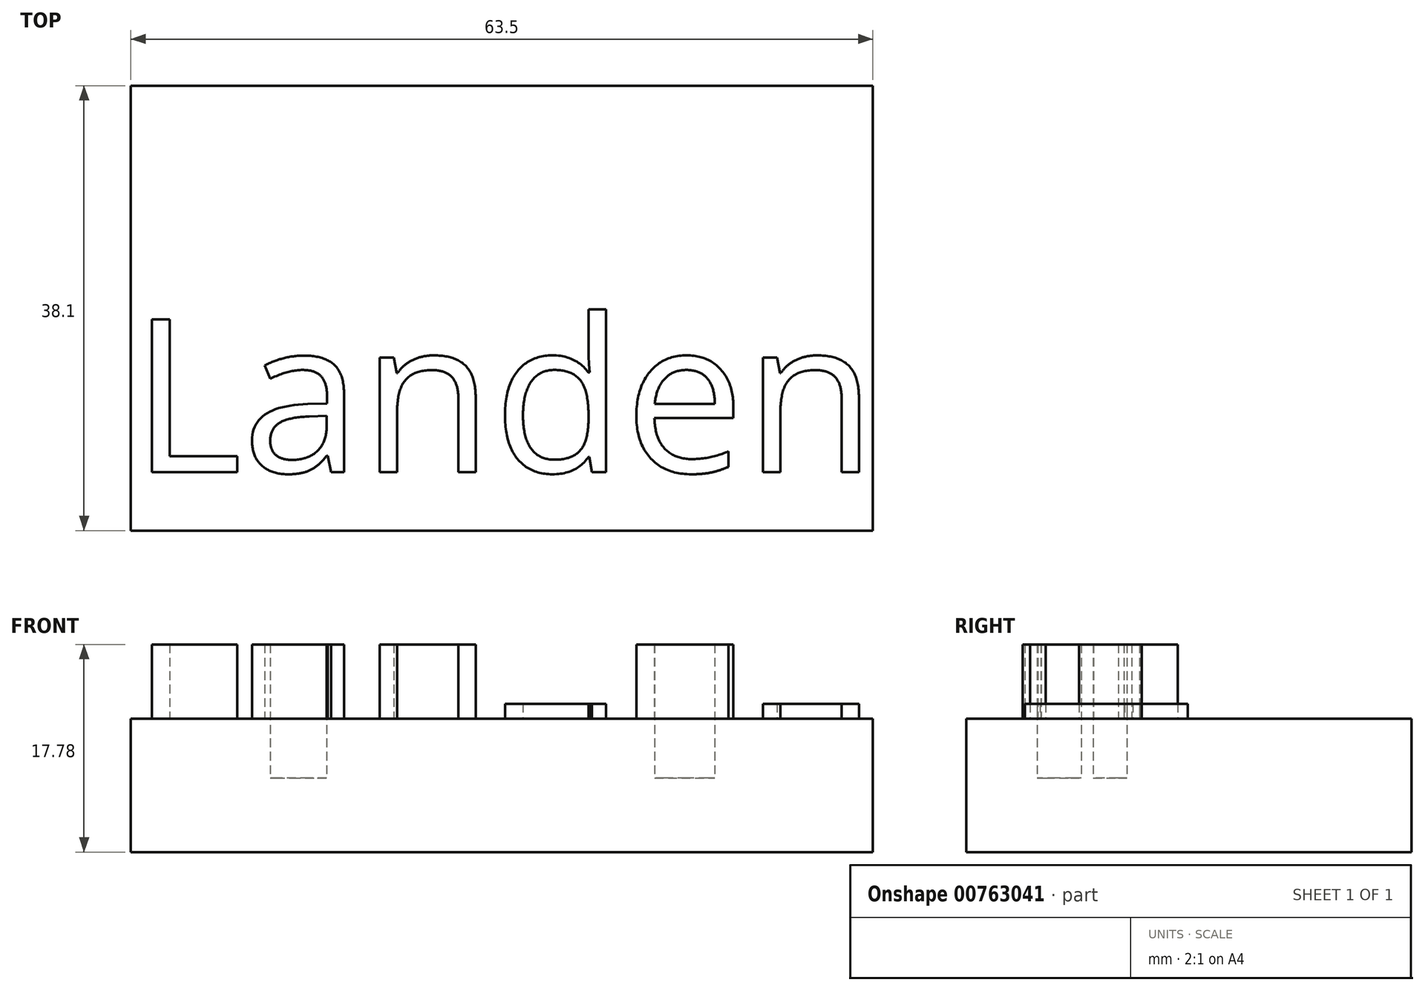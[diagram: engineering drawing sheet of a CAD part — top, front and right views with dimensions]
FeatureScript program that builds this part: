
annotation { "Feature Type Name" : "Feature", "Feature Type Description" : "" }
export const myFeature = defineFeature(function(context is Context, id is Id, definition is map)
    precondition{}
    {
        {
            var Q0;
            Q0=qCreatedBy(makeId("Top.planeOp"),FACE);
            var sketch = newSketch(context, id + "F0", { "sketchPlane" : qUnion([Q0])});
            skLineSegment(sketch, "E0.bottom", {"start": v(0, 0) * mm, "end": v(63.5, 0) * mm});
            skLineSegment(sketch, "E0.top", {"start": v(0, 38.1) * mm, "end": v(63.5, 38.1) * mm});
            skLineSegment(sketch, "E0.left", {"start": v(0, 0) * mm, "end": v(0, 38.1) * mm});
            skLineSegment(sketch, "E0.right", {"start": v(63.5, 0) * mm, "end": v(63.5, 38.1) * mm});
            skSolve(sketch);
        }
        {
            var Q0;
            Q0=makeQuery(id+"F0.imprint","IMPRINT",FACE,{"disambiguationData":[TD([[makeQuery(id+"F0.imprint","IMPRINT",EDGE,{"derivedFrom":sQuery(id+"F0.wireOp",EDGE,"E0.bottom")}),1.0]])]});
            extrude(context, id + "F1", {"entities" : qUnion([Q0]), "depth" : 6.35 * mm, "offsetDistance" : 25.4 * mm});
        }
        {
            var Q0;
            Q0=makeQuery(id+"F1.opExtrude","CAP_FACE",FACE,{"disambiguationData":[OSD([sQuery(id+"F0.wireOp",EDGE,"E0.bottom"),sQuery(id+"F0.wireOp",EDGE,"E0.top"),sQuery(id+"F0.wireOp",EDGE,"E0.left"),sQuery(id+"F0.wireOp",EDGE,"E0.right")])],"isStart":false});
            var sketch = newSketch(context, id + "F2", { "sketchPlane" : qUnion([Q0])});
            skText(sketch, "E1", { "text": "Landen", "fontName": "OpenSans-Regular.ttf"});
            const initialGuessF2  = {"E1": [0, 0.005, 1, 0, 0.01321]};
            skSetInitialGuess(sketch, initialGuessF2);
            skSolve(sketch);
        }
        {
            var Q0;
            Q0 = qSketchRegion(id + "F2", true);
            extrude(context, id + "F3", {"entities" : qUnion([Q0]), "operationType" : NewBodyOperationType.ADD, "depth" : 6.35 * mm, "offsetDistance" : 25.4 * mm});
        }
        {
            var Q0;
            Q0 = qSketchRegion(id + "F2", true);
            extrude(context, id + "F4", {"entities" : qUnion([Q0]), "operationType" : NewBodyOperationType.ADD, "depth" : 5.08 * mm, "offsetDistance" : 25.4 * mm});
        }
        {
            var Q0;
            Q0=makeQuery(id+"F3.opExtrude","CAP_FACE",FACE,{"disambiguationData":[OSD([sQuery(id+"F2.wireOp",EDGE,"E1.sketch_text.stroke-0"),sQuery(id+"F2.wireOp",EDGE,"E1.sketch_text.stroke-1"),sQuery(id+"F2.wireOp",EDGE,"E1.sketch_text.stroke-2"),sQuery(id+"F2.wireOp",EDGE,"E1.sketch_text.stroke-3"),sQuery(id+"F2.wireOp",EDGE,"E1.sketch_text.stroke-4"),sQuery(id+"F2.wireOp",EDGE,"E1.sketch_text.stroke-5")])],"isStart":false});
            var Q1;
            Q1=makeQuery(id+"F3.opExtrude","CAP_FACE",FACE,{"disambiguationData":[OSD([sQuery(id+"F2.wireOp",EDGE,"E1.sketch_text.stroke-6"),sQuery(id+"F2.wireOp",EDGE,"E1.sketch_text.stroke-7"),sQuery(id+"F2.wireOp",EDGE,"E1.sketch_text.stroke-8"),sQuery(id+"F2.wireOp",EDGE,"E1.sketch_text.stroke-9"),sQuery(id+"F2.wireOp",EDGE,"E1.sketch_text.stroke-10"),sQuery(id+"F2.wireOp",EDGE,"E1.sketch_text.stroke-11"),sQuery(id+"F2.wireOp",EDGE,"E1.sketch_text.stroke-12"),sQuery(id+"F2.wireOp",EDGE,"E1.sketch_text.stroke-13"),sQuery(id+"F2.wireOp",EDGE,"E1.sketch_text.stroke-14"),sQuery(id+"F2.wireOp",EDGE,"E1.sketch_text.stroke-15"),sQuery(id+"F2.wireOp",EDGE,"E1.sketch_text.stroke-16"),sQuery(id+"F2.wireOp",EDGE,"E1.sketch_text.stroke-17"),sQuery(id+"F2.wireOp",EDGE,"E1.sketch_text.stroke-18"),sQuery(id+"F2.wireOp",EDGE,"E1.sketch_text.stroke-19"),sQuery(id+"F2.wireOp",EDGE,"E1.sketch_text.stroke-20"),sQuery(id+"F2.wireOp",EDGE,"E1.sketch_text.stroke-21"),sQuery(id+"F2.wireOp",EDGE,"E1.sketch_text.stroke-22"),sQuery(id+"F2.wireOp",EDGE,"E1.sketch_text.stroke-23"),sQuery(id+"F2.wireOp",EDGE,"E1.sketch_text.stroke-24"),sQuery(id+"F2.wireOp",EDGE,"E1.sketch_text.stroke-25"),sQuery(id+"F2.wireOp",EDGE,"E1.sketch_text.stroke-26"),sQuery(id+"F2.wireOp",EDGE,"E1.sketch_text.stroke-27"),sQuery(id+"F2.wireOp",EDGE,"E1.sketch_text.stroke-28"),sQuery(id+"F2.wireOp",EDGE,"E1.sketch_text.stroke-29"),sQuery(id+"F2.wireOp",EDGE,"E1.sketch_text.stroke-30"),sQuery(id+"F2.wireOp",EDGE,"E1.sketch_text.stroke-31"),sQuery(id+"F2.wireOp",EDGE,"E1.sketch_text.stroke-32")])],"isStart":false});
            var Q2;
            {var subQ0=sQuery(id+"F0.wireOp",EDGE,"E0.left");var subQ1=sQuery(id+"F0.wireOp",EDGE,"E0.bottom");var subQ2=sQuery(id+"F0.wireOp",EDGE,"E0.right");var subQ3=sQuery(id+"F0.wireOp",EDGE,"E0.top");Q2=makeQuery(id+"F3.boolean.opBoolean","SPLIT",FACE,{"disambiguationData":[TD([makeQuery(id+"F1.opExtrude","SWEPT_FACE",FACE,{"disambiguationData":[OSD([subQ1])]})])],"derivedFrom":makeQuery(id+"F1.opExtrude","CAP_FACE",FACE,{"disambiguationData":[OSD([subQ1,subQ3,subQ0,subQ2])],"isStart":false})});}
            var Q3;
            Q3=makeQuery(id+"F3.opExtrude","CAP_FACE",FACE,{"disambiguationData":[OSD([sQuery(id+"F2.wireOp",EDGE,"E1.sketch_text.stroke-33"),sQuery(id+"F2.wireOp",EDGE,"E1.sketch_text.stroke-34"),sQuery(id+"F2.wireOp",EDGE,"E1.sketch_text.stroke-35"),sQuery(id+"F2.wireOp",EDGE,"E1.sketch_text.stroke-36"),sQuery(id+"F2.wireOp",EDGE,"E1.sketch_text.stroke-37"),sQuery(id+"F2.wireOp",EDGE,"E1.sketch_text.stroke-38"),sQuery(id+"F2.wireOp",EDGE,"E1.sketch_text.stroke-39"),sQuery(id+"F2.wireOp",EDGE,"E1.sketch_text.stroke-40"),sQuery(id+"F2.wireOp",EDGE,"E1.sketch_text.stroke-41"),sQuery(id+"F2.wireOp",EDGE,"E1.sketch_text.stroke-42"),sQuery(id+"F2.wireOp",EDGE,"E1.sketch_text.stroke-43"),sQuery(id+"F2.wireOp",EDGE,"E1.sketch_text.stroke-44"),sQuery(id+"F2.wireOp",EDGE,"E1.sketch_text.stroke-45"),sQuery(id+"F2.wireOp",EDGE,"E1.sketch_text.stroke-46"),sQuery(id+"F2.wireOp",EDGE,"E1.sketch_text.stroke-47"),sQuery(id+"F2.wireOp",EDGE,"E1.sketch_text.stroke-48"),sQuery(id+"F2.wireOp",EDGE,"E1.sketch_text.stroke-49")])],"isStart":false});
            var Q4;
            Q4=makeQuery(id+"F3.boolean.opBoolean","SPLIT",FACE,{"disambiguationData":[TD([makeQuery(id+"F3.opExtrude","SWEPT_FACE",FACE,{"disambiguationData":[OSD([sQuery(id+"F2.wireOp",EDGE,"E1.sketch_text.stroke-65")])]})])],"derivedFrom":makeQuery(id+"F1.opExtrude","CAP_FACE",FACE,{"disambiguationData":[OSD([sQuery(id+"F0.wireOp",EDGE,"E0.bottom"),sQuery(id+"F0.wireOp",EDGE,"E0.top"),sQuery(id+"F0.wireOp",EDGE,"E0.left"),sQuery(id+"F0.wireOp",EDGE,"E0.right")])],"isStart":false})});
            var Q5;
            Q5=makeQuery(id+"F3.opExtrude","CAP_FACE",FACE,{"disambiguationData":[OSD([sQuery(id+"F2.wireOp",EDGE,"E1.sketch_text.stroke-74"),sQuery(id+"F2.wireOp",EDGE,"E1.sketch_text.stroke-75"),sQuery(id+"F2.wireOp",EDGE,"E1.sketch_text.stroke-76"),sQuery(id+"F2.wireOp",EDGE,"E1.sketch_text.stroke-77"),sQuery(id+"F2.wireOp",EDGE,"E1.sketch_text.stroke-78"),sQuery(id+"F2.wireOp",EDGE,"E1.sketch_text.stroke-79"),sQuery(id+"F2.wireOp",EDGE,"E1.sketch_text.stroke-80"),sQuery(id+"F2.wireOp",EDGE,"E1.sketch_text.stroke-81"),sQuery(id+"F2.wireOp",EDGE,"E1.sketch_text.stroke-82"),sQuery(id+"F2.wireOp",EDGE,"E1.sketch_text.stroke-83"),sQuery(id+"F2.wireOp",EDGE,"E1.sketch_text.stroke-84"),sQuery(id+"F2.wireOp",EDGE,"E1.sketch_text.stroke-85"),sQuery(id+"F2.wireOp",EDGE,"E1.sketch_text.stroke-86"),sQuery(id+"F2.wireOp",EDGE,"E1.sketch_text.stroke-87"),sQuery(id+"F2.wireOp",EDGE,"E1.sketch_text.stroke-88"),sQuery(id+"F2.wireOp",EDGE,"E1.sketch_text.stroke-89"),sQuery(id+"F2.wireOp",EDGE,"E1.sketch_text.stroke-90"),sQuery(id+"F2.wireOp",EDGE,"E1.sketch_text.stroke-91"),sQuery(id+"F2.wireOp",EDGE,"E1.sketch_text.stroke-92")])],"isStart":false});
            extrude(context, id + "F5", {"entities" : qUnion([Q0, Q1, Q2, Q3, Q4, Q5]), "operationType" : NewBodyOperationType.ADD, "depth" : 5.08 * mm, "offsetDistance" : 25.4 * mm});
        }
    });
